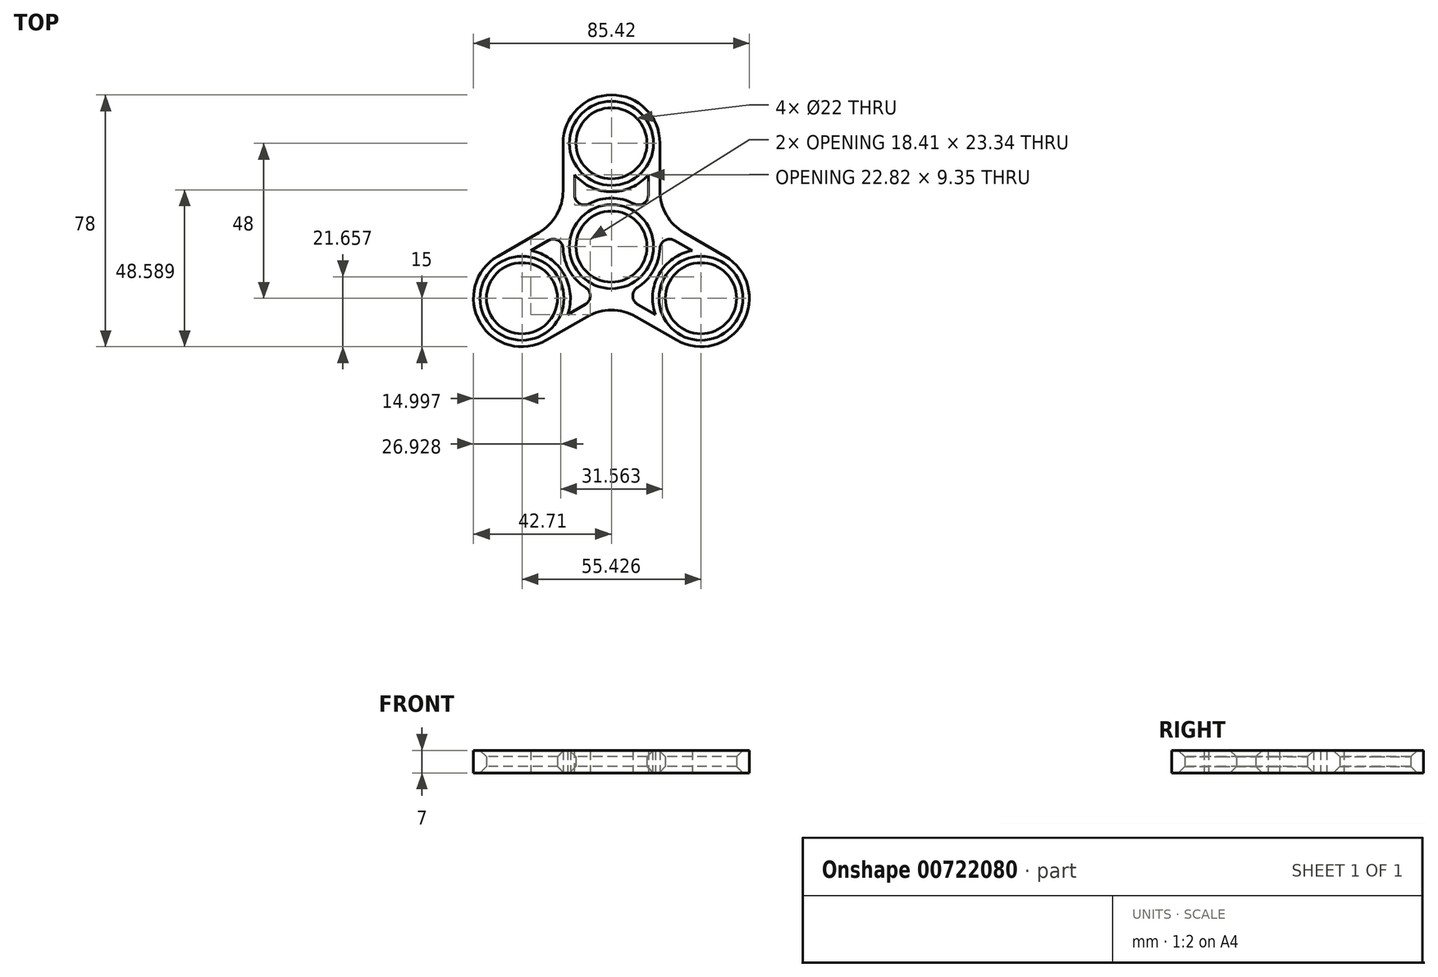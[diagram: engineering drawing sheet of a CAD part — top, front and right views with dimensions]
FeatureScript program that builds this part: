
annotation { "Feature Type Name" : "Feature", "Feature Type Description" : "" }
export const myFeature = defineFeature(function(context is Context, id is Id, definition is map)
    precondition{}
    {
        {
            var Q0;
            Q0=qCreatedBy(makeId("Top.planeOp"),FACE);
            var sketch = newSketch(context, id + "F0", { "sketchPlane" : qUnion([Q0])});
            skCircle(sketch, "E0", {"center": v(0, 0) * mm, "radius": 11 * mm});
            skCircle(sketch, "E1", {"center": v(0, 0) * mm, "radius": 15 * mm});
            skCircle(sketch, "E2", {"center": v(0, 32) * mm, "radius": 11 * mm});
            skCircle(sketch, "E3", {"center": v(0, 32) * mm, "radius": 15 * mm});
            skLineSegment(sketch, "E4.bottom", {"start": v(-15, 32) * mm, "end": v(15, 32) * mm});
            skLineSegment(sketch, "E4.top", {"start": v(-15, 0) * mm, "end": v(15, 0) * mm});
            skLineSegment(sketch, "E4.left", {"start": v(-15, 32) * mm, "end": v(-15, 0) * mm});
            skLineSegment(sketch, "E4.right", {"start": v(15, 32) * mm, "end": v(15, 0) * mm});
            skLineSegment(sketch, "E5.bottom", {"start": v(11.41, 9.74) * mm, "end": v(-11.41, 9.74) * mm, "construction": true});
            skLineSegment(sketch, "E5.top", {"start": v(11.41, 22.26) * mm, "end": v(-11.41, 22.26) * mm, "construction": true});
            skLineSegment(sketch, "E5.left", {"start": v(11.41, 9.74) * mm, "end": v(11.41, 22.26) * mm});
            skLineSegment(sketch, "E5.right", {"start": v(-11.41, 9.74) * mm, "end": v(-11.41, 22.26) * mm});
            skCircle(sketch, "E6.1.0", {"center": v(-27.71, -16) * mm, "radius": 11 * mm});
            skCircle(sketch, "E6.1.1", {"center": v(-27.71, -16) * mm, "radius": 15 * mm});
            skLineSegment(sketch, "E6.1.2", {"start": v(-35.21, -3) * mm, "end": v(-7.5, 13) * mm});
            skLineSegment(sketch, "E6.1.3", {"start": v(-14.14, 5.01) * mm, "end": v(-24.99, -1.25) * mm});
            skLineSegment(sketch, "E6.1.4", {"start": v(-2.73, -14.75) * mm, "end": v(-13.58, -21.01) * mm});
            skLineSegment(sketch, "E6.1.5", {"start": v(-20.21, -29) * mm, "end": v(7.5, -13) * mm});
            skCircle(sketch, "E6.2.0", {"center": v(27.71, -16) * mm, "radius": 11 * mm});
            skCircle(sketch, "E6.2.1", {"center": v(27.71, -16) * mm, "radius": 15 * mm});
            skLineSegment(sketch, "E6.2.2", {"start": v(20.21, -29) * mm, "end": v(-7.5, -13) * mm});
            skLineSegment(sketch, "E6.2.3", {"start": v(2.73, -14.75) * mm, "end": v(13.58, -21.01) * mm});
            skLineSegment(sketch, "E6.2.4", {"start": v(14.14, 5.01) * mm, "end": v(24.99, -1.25) * mm});
            skLineSegment(sketch, "E6.2.5", {"start": v(35.21, -3) * mm, "end": v(7.5, 13) * mm});
            skSolve(sketch);
        }
        {
            var Q0;
            Q0 = qSketchRegion(id + "F0", true);
            var Q1;
            {var subQ3=sQuery(id+"F0.wireOp",EDGE,"E4.top");var subQ6=sQuery(id+"F0.wireOp",EDGE,"E0");var subQ7=makeQuery(id+"F0.imprint","INTERSECT",VERTEX,{"disambiguationData":[OD(0.0)],"derivedFrom":[subQ6,subQ3]});Q1=makeQuery(id+"F0.imprint","IMPRINT",FACE,{"disambiguationData":[TD([[makeQuery(id+"F0.imprint","IMPRINT",EDGE,{"disambiguationData":[TD([[subQ7,-1.0]])],"derivedFrom":subQ6}),-1.0]])]});}
            var Q2;
            {var subQ4=sQuery(id+"F0.wireOp",EDGE,"E4.top");var subQ6=sQuery(id+"F0.wireOp",EDGE,"E0");var subQ8=makeQuery(id+"F0.imprint","INTERSECT",VERTEX,{"disambiguationData":[OD(0.0)],"derivedFrom":[subQ6,subQ4]});Q2=makeQuery(id+"F0.imprint","IMPRINT",FACE,{"disambiguationData":[TD([[makeQuery(id+"F0.imprint","IMPRINT",EDGE,{"disambiguationData":[TD([[subQ8,1.0]])],"derivedFrom":subQ6}),-1.0]])]});}
            extrude(context, id + "F1", {"entities" : qUnion([Q0, Q1, Q2]), "depth" : 7 * mm, "offsetDistance" : 25 * mm});
        }
        {
            var Q0;
            Q0=makeQuery(id+"F1.opExtrude","CAP_EDGE",EDGE,{"disambiguationData":[OSD([sQuery(id+"F0.wireOp",EDGE,"E0")])],"isStart":false});
            var Q1;
            Q1=makeQuery(id+"F1.opExtrude","CAP_EDGE",EDGE,{"disambiguationData":[OSD([sQuery(id+"F0.wireOp",EDGE,"E2")])],"isStart":false});
            var Q2;
            Q2=makeQuery(id+"F1.opExtrude","CAP_EDGE",EDGE,{"disambiguationData":[OSD([sQuery(id+"F0.wireOp",EDGE,"E6.2.0")])],"isStart":false});
            var Q3;
            Q3=makeQuery(id+"F1.opExtrude","CAP_EDGE",EDGE,{"disambiguationData":[OSD([sQuery(id+"F0.wireOp",EDGE,"E6.2.0")])],"isStart":true});
            var Q4;
            Q4=makeQuery(id+"F1.opExtrude","CAP_EDGE",EDGE,{"disambiguationData":[OSD([sQuery(id+"F0.wireOp",EDGE,"E2")])],"isStart":true});
            var Q5;
            Q5=makeQuery(id+"F1.opExtrude","CAP_EDGE",EDGE,{"disambiguationData":[OSD([sQuery(id+"F0.wireOp",EDGE,"E0")])],"isStart":true});
            var Q6;
            Q6=makeQuery(id+"F1.opExtrude","CAP_EDGE",EDGE,{"disambiguationData":[OSD([sQuery(id+"F0.wireOp",EDGE,"E6.1.0")])],"isStart":true});
            var Q7;
            Q7=makeQuery(id+"F1.opExtrude","CAP_EDGE",EDGE,{"disambiguationData":[OSD([sQuery(id+"F0.wireOp",EDGE,"E6.1.0")])],"isStart":false});
            chamfer(context, id + "F2", {"entities" : qUnion([Q0, Q1, Q2, Q3, Q4, Q5, Q6, Q7]), "width" : 2 * mm, "tangentPropagation" : true});
        }
        {
            var Q0;
            Q0=makeQuery(id+"F1.opExtrude","SWEPT_EDGE",EDGE,{"disambiguationData":[OSD([sQuery(id+"F0.wireOp",EDGE,"E6.1.5"),sQuery(id+"F0.wireOp",EDGE,"E6.2.2")])]});
            var Q1;
            Q1=makeQuery(id+"F1.opExtrude","SWEPT_EDGE",EDGE,{"disambiguationData":[OSD([sQuery(id+"F0.wireOp",EDGE,"E4.right"),sQuery(id+"F0.wireOp",EDGE,"E6.2.5")])]});
            var Q2;
            Q2=makeQuery(id+"F1.opExtrude","SWEPT_EDGE",EDGE,{"disambiguationData":[OSD([sQuery(id+"F0.wireOp",EDGE,"E4.left"),sQuery(id+"F0.wireOp",EDGE,"E6.1.2")])]});
            fillet(context, id + "F3", {"entities" : qUnion([Q0, Q1, Q2]), "radius" : 15 * mm, "tangentPropagation" : true, "allowEdgeOverflow" : false});
        }
        {
            var Q0;
            Q0=makeQuery(id+"F1.opExtrude","SWEPT_EDGE",EDGE,{"disambiguationData":[OSD([sQuery(id+"F0.wireOp",EDGE,"E1"),sQuery(id+"F0.wireOp",EDGE,"E5.right")])]});
            var Q1;
            Q1=makeQuery(id+"F1.opExtrude","SWEPT_EDGE",EDGE,{"disambiguationData":[OSD([sQuery(id+"F0.wireOp",EDGE,"E1"),sQuery(id+"F0.wireOp",EDGE,"E5.left")])]});
            var Q2;
            Q2=makeQuery(id+"F1.opExtrude","SWEPT_EDGE",EDGE,{"disambiguationData":[OSD([sQuery(id+"F0.wireOp",EDGE,"E1"),sQuery(id+"F0.wireOp",EDGE,"E6.2.4")])]});
            var Q3;
            Q3=makeQuery(id+"F1.opExtrude","SWEPT_EDGE",EDGE,{"disambiguationData":[OSD([sQuery(id+"F0.wireOp",EDGE,"E1"),sQuery(id+"F0.wireOp",EDGE,"E6.1.3")])]});
            var Q4;
            Q4=makeQuery(id+"F1.opExtrude","SWEPT_EDGE",EDGE,{"disambiguationData":[OSD([sQuery(id+"F0.wireOp",EDGE,"E1"),sQuery(id+"F0.wireOp",EDGE,"E6.2.3")])]});
            var Q5;
            Q5=makeQuery(id+"F1.opExtrude","SWEPT_EDGE",EDGE,{"disambiguationData":[OSD([sQuery(id+"F0.wireOp",EDGE,"E1"),sQuery(id+"F0.wireOp",EDGE,"E6.1.4")])]});
            fillet(context, id + "F4", {"entities" : qUnion([Q0, Q1, Q2, Q3, Q4, Q5]), "radius" : 3 * mm, "tangentPropagation" : true, "allowEdgeOverflow" : false});
        }
    });
